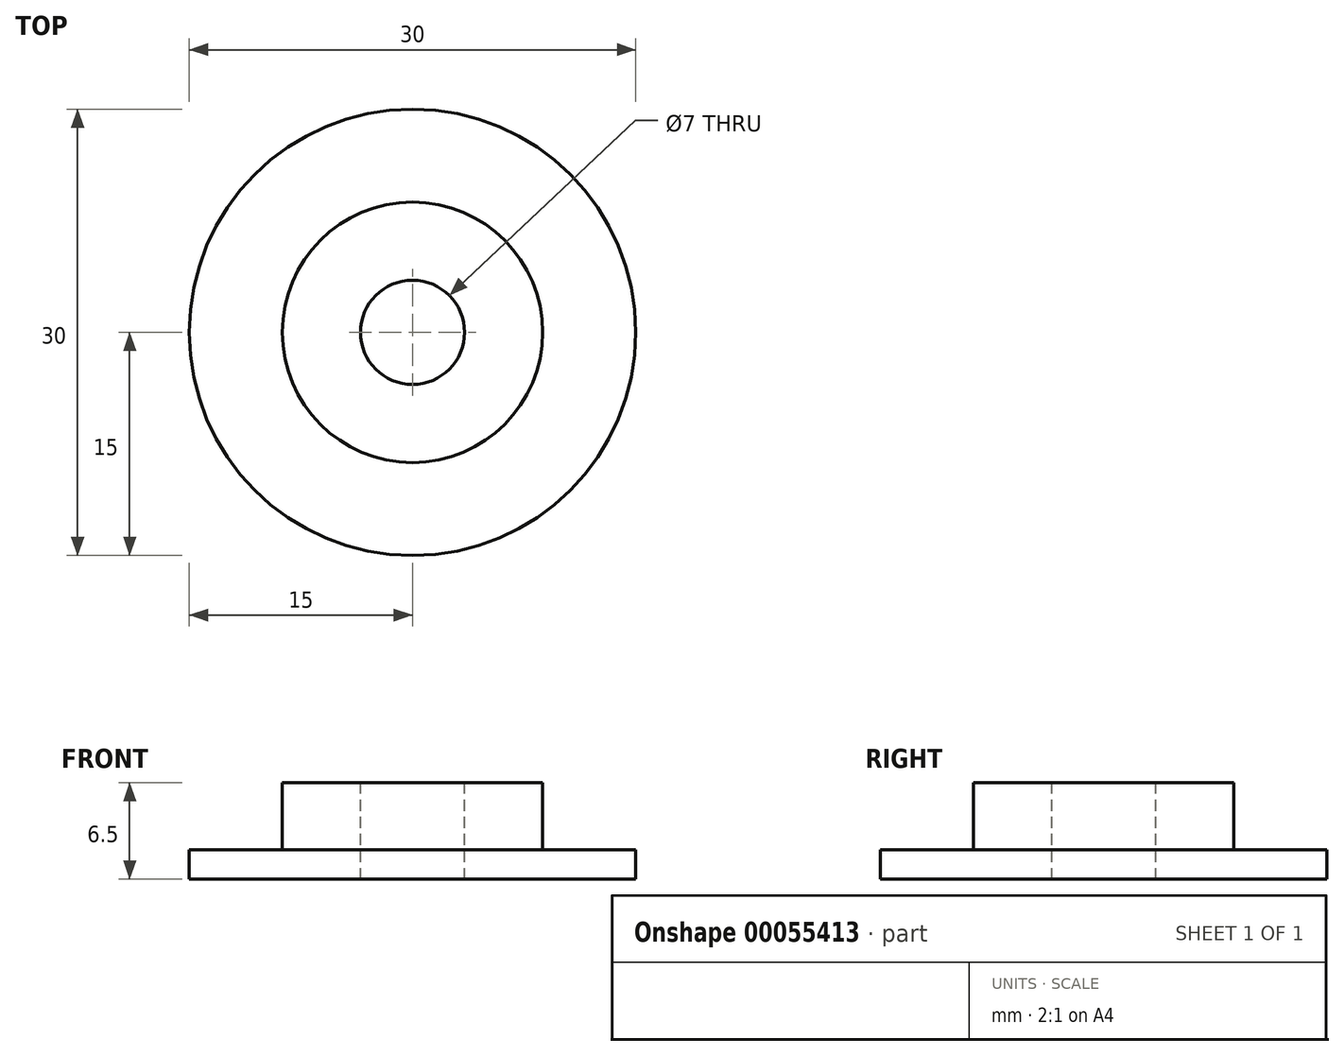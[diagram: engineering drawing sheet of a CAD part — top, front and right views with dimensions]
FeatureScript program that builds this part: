
annotation { "Feature Type Name" : "Feature", "Feature Type Description" : "" }
export const myFeature = defineFeature(function(context is Context, id is Id, definition is map)
    precondition{}
    {
        {
            var Q0;
            Q0=qCreatedBy(makeId("Front.planeOp"),FACE);
            var sketch = newSketch(context, id + "F0", { "sketchPlane" : qUnion([Q0])});
            skLineSegment(sketch, "E0", {"start": v(-15, 0) * mm, "end": v(-15, 2) * mm});
            skLineSegment(sketch, "E1", {"start": v(-15, 2) * mm, "end": v(-8.75, 2) * mm});
            skLineSegment(sketch, "E2", {"start": v(-8.75, 2) * mm, "end": v(-8.75, 6.5) * mm});
            skLineSegment(sketch, "E3", {"start": v(-8.75, 6.5) * mm, "end": v(-3.5, 6.5) * mm});
            skLineSegment(sketch, "E4", {"start": v(-3.5, 6.5) * mm, "end": v(-3.5, 0) * mm});
            skLineSegment(sketch, "E5", {"start": v(-3.5, 0) * mm, "end": v(-15, 0) * mm});
            skLineSegment(sketch, "E6", {"start": v(0, 30.91) * mm, "end": v(0, -20.93) * mm, "construction": true});
            skSolve(sketch);
        }
        {
            var Q0;
            Q0=makeQuery(id+"F0.imprint","IMPRINT",FACE,{"disambiguationData":[TD([[makeQuery(id+"F0.imprint","IMPRINT",EDGE,{"derivedFrom":sQuery(id+"F0.wireOp",EDGE,"E0")}),-1.0]])]});
            var Q1;
            Q1=sQuery(id+"F0.wireOp",EDGE,"E6");
            revolve(context, id + "F1", {"entities" : qUnion([Q0]), "axis" : qUnion([Q1]), "revolveType" : RevolveType.FULL});
        }
    });
